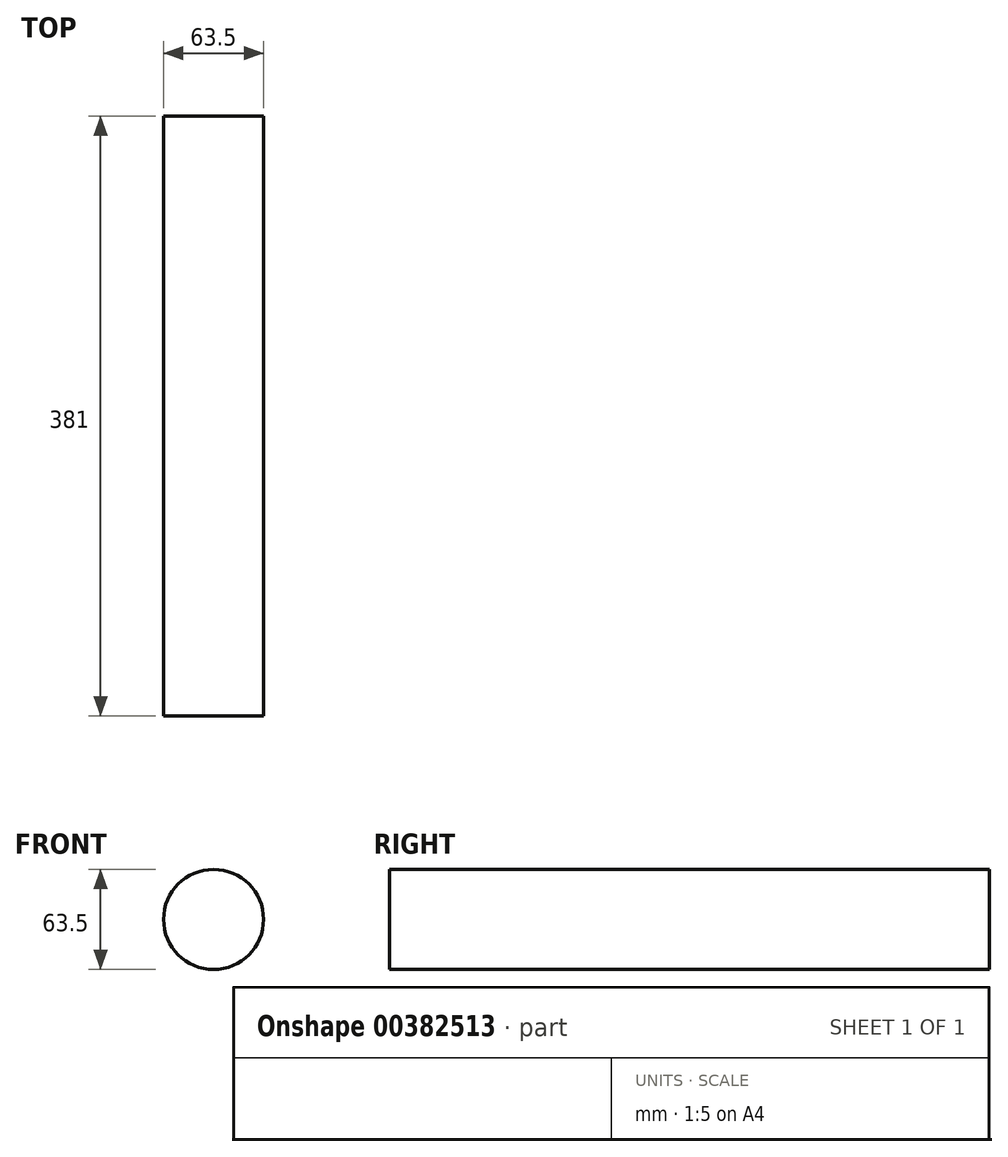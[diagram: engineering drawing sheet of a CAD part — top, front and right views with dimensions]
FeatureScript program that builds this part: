
annotation { "Feature Type Name" : "Feature", "Feature Type Description" : "" }
export const myFeature = defineFeature(function(context is Context, id is Id, definition is map)
    precondition{}
    {
        {
            var Q0;
            Q0=qCreatedBy(makeId("Front.planeOp"),FACE);
            var sketch = newSketch(context, id + "F0", { "sketchPlane" : qUnion([Q0])});
            skCircle(sketch, "E0", {"center": v(-49.65, 18.3) * mm, "radius": 31.75 * mm});
            skSolve(sketch);
        }
        {
            var Q0;
            Q0 = qSketchRegion(id + "F0", true);
            extrude(context, id + "F1", {"entities" : qUnion([Q0]), "depth" : 381 * mm});
        }
    });
